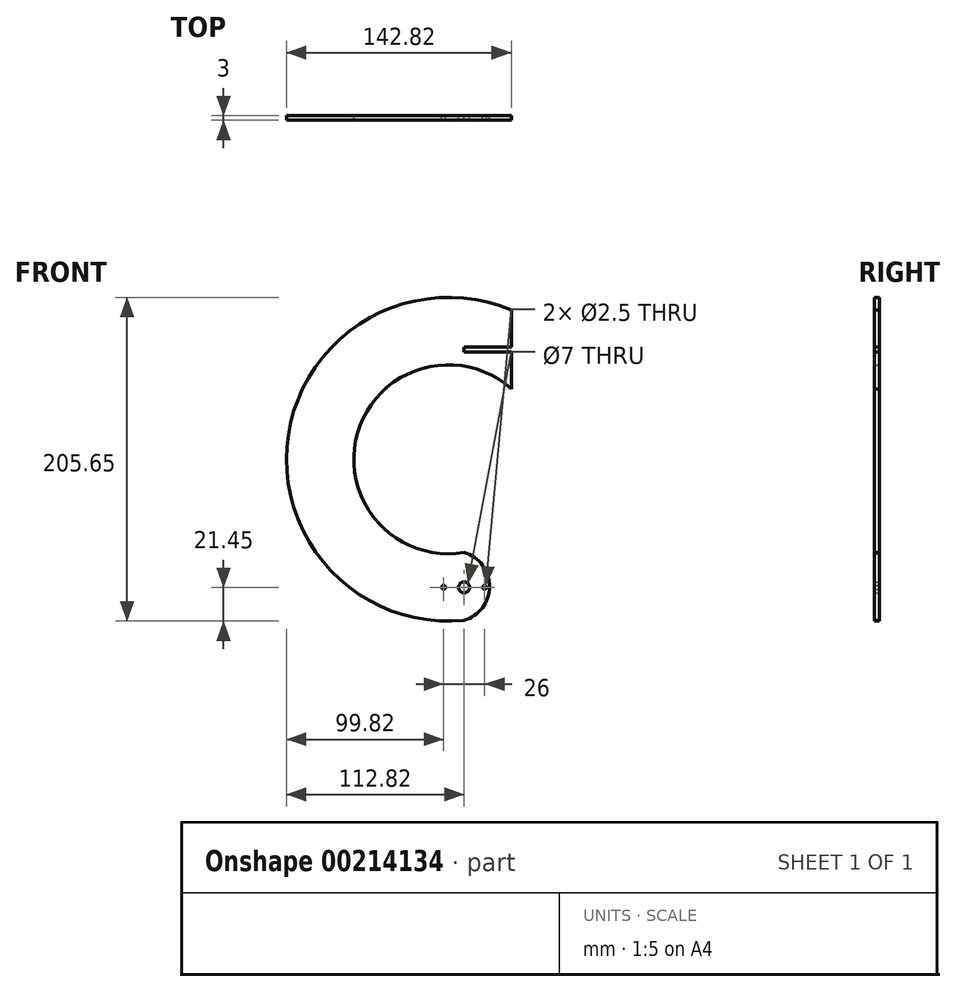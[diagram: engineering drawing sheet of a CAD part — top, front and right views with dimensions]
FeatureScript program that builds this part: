
annotation { "Feature Type Name" : "Feature", "Feature Type Description" : "" }
export const myFeature = defineFeature(function(context is Context, id is Id, definition is map)
    precondition{}
    {
        {
            var Q0;
            Q0=qCreatedBy(makeId("Front.planeOp"),FACE);
            var sketch = newSketch(context, id + "F0", { "sketchPlane" : qUnion([Q0])});
            skCircle(sketch, "E0", {"center": v(0, 0) * mm, "radius": 3.5 * mm});
            skCircle(sketch, "E1", {"center": v(13, 0) * mm, "radius": 1.25 * mm});
            skCircle(sketch, "E2", {"center": v(-13, 0) * mm, "radius": 1.25 * mm});
            skLineSegment(sketch, "E3", {"start": v(30, 126.1) * mm, "end": v(30, 176.1) * mm});
            skArc(sketch, "E4", {"start": v(30, 176.1) * mm, "mid": v(-111.64, 96.93) * mm, "end": v(-0.17, -20.97) * mm});
            skLineSegment(sketch, "E5.bottom", {"start": v(30, 152.6) * mm, "end": v(0, 152.6) * mm});
            skLineSegment(sketch, "E5.top", {"start": v(30, 149.6) * mm, "end": v(0, 149.6) * mm});
            skLineSegment(sketch, "E5.left", {"start": v(30, 149.6) * mm, "end": v(30, 152.6) * mm});
            skLineSegment(sketch, "E5.right", {"start": v(0, 149.6) * mm, "end": v(0, 152.6) * mm});
            skArc(sketch, "E6", {"start": v(30, 126.1) * mm, "mid": v(-67.64, 98.02) * mm, "end": v(0, 22.21) * mm});
            skLineSegment(sketch, "E7", {"start": v(-0.17, 18.66) * mm, "end": v(-0.17, -20.97) * mm});
            skArc(sketch, "E8", {"start": v(-0.17, -20.97) * mm, "mid": v(16.14, 0.56) * mm, "end": v(0, 22.21) * mm});
            skSolve(sketch);
        }
        {
            var Q0;
            Q0=makeQuery(id+"F0.imprint","IMPRINT",FACE,{"disambiguationData":[TD([[makeQuery(id+"F0.imprint","IMPRINT",EDGE,{"derivedFrom":sQuery(id+"F0.wireOp",EDGE,"E1")}),-1.0]])]});
            extrude(context, id + "F1", {"entities" : qUnion([Q0]), "depth" : 3 * mm});
        }
    });
